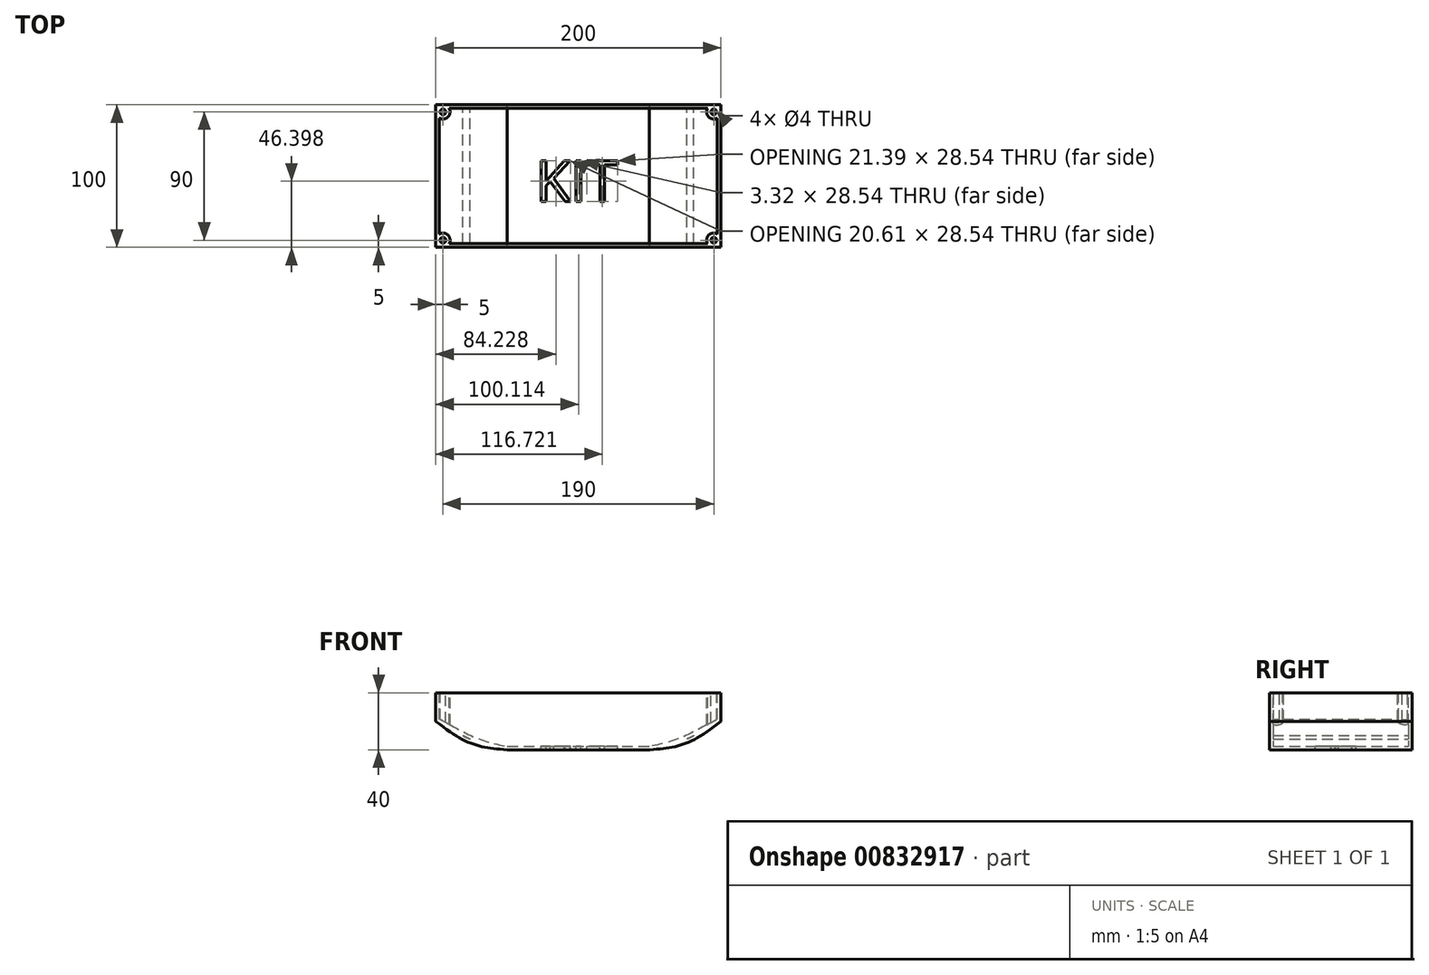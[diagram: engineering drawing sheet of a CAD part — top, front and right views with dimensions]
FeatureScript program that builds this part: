
annotation { "Feature Type Name" : "Feature", "Feature Type Description" : "" }
export const myFeature = defineFeature(function(context is Context, id is Id, definition is map)
    precondition{}
    {
        {
            var Q0;
            Q0=qCreatedBy(makeId("Front.planeOp"),FACE);
            var sketch = newSketch(context, id + "F0", { "sketchPlane" : qUnion([Q0])});
            skLineSegment(sketch, "E0.bottom", {"start": v(-100, 20) * mm, "end": v(100, 20) * mm});
            skLineSegment(sketch, "E0.top", {"start": v(-50, -20) * mm, "end": v(50, -20) * mm});
            skLineSegment(sketch, "E0.left", {"start": v(-100, 20) * mm, "end": v(-100, 0) * mm});
            skLineSegment(sketch, "E0.right", {"start": v(100, 20) * mm, "end": v(100, 0) * mm});
            skFitSpline(sketch, "E1", {"points": [v(-100, 0) * mm, v(-50, -20) * mm, v(50, -20) * mm, v(100, 0) * mm], "startDerivative": vector(217.09, -116.87) * mm, "endDerivative": vector(211.84, 170.9) * mm});
            skPoint(sketch, "E2.orphan", {"position": v(-100, -20) * mm});
            skPoint(sketch, "E3.orphan", {"position": v(100, -20) * mm});
            skSolve(sketch);
        }
        {
            var Q0;
            Q0=makeQuery(id+"F0.imprint","IMPRINT",FACE,{"disambiguationData":[TD([[makeQuery(id+"F0.imprint","IMPRINT",EDGE,{"derivedFrom":sQuery(id+"F0.wireOp",EDGE,"E0.bottom")}),-1.0]])]});
            extrude(context, id + "F1", {"entities" : qUnion([Q0]), "endBound" : BoundingType.SYMMETRIC, "depth" : 100 * mm, "offsetDistance" : 25 * mm});
        }
        {
            var Q0;
            Q0=makeQuery(id+"F1.opExtrude","SWEPT_FACE",FACE,{"disambiguationData":[OSD([sQuery(id+"F0.wireOp",EDGE,"E0.bottom")])]});
            shell(context, id + "F2", {"entities" : qUnion([Q0]), "thickness" : 2.5 * mm});
        }
        {
            var Q0;
            Q0=makeQuery(id+"F1.opExtrude","SWEPT_FACE",FACE,{"disambiguationData":[OSD([sQuery(id+"F0.wireOp",EDGE,"E0.bottom")])]});
            var sketch = newSketch(context, id + "F3", { "sketchPlane" : qUnion([Q0])});
            skCircle(sketch, "E4", {"center": v(-95, -45) * mm, "radius": 2 * mm});
            skCircle(sketch, "E5", {"center": v(-95, -45) * mm, "radius": 5 * mm});
            skSolve(sketch);
        }
        {
            var Q0;
            Q0 = qSketchRegion(id + "F3", true);
            extrude(context, id + "F4", {"entities" : qUnion([Q0]), "operationType" : NewBodyOperationType.ADD, "endBound" : BoundingType.UP_TO_NEXT, "oppositeDirection" : true, "depth" : 25 * mm, "offsetDistance" : 25 * mm});
        }
        {
            var Q0;
            Q0=makeQuery(id+"F1.opExtrude","SWEPT_BODY",BODY,{"disambiguationData":[OSD([sQuery(id+"F0.wireOp",EDGE,"E0.bottom"),sQuery(id+"F0.wireOp",EDGE,"E0.top"),sQuery(id+"F0.wireOp",EDGE,"E0.left"),sQuery(id+"F0.wireOp",EDGE,"E0.right"),sQuery(id+"F0.wireOp",EDGE,"E1"),sQuery(id+"F0.wireOp",EDGE,"E1")])]});
            var Q1;
            Q1=qCreatedBy(makeId("Right.planeOp"),FACE);
            mirror(context, id + "F5", {"operationType" : NewBodyOperationType.ADD, "entities" : qUnion([Q0]), "mirrorPlane" : qUnion([Q1])});
        }
        {
            var Q0;
            Q0=makeQuery(id+"F1.opExtrude","SWEPT_BODY",BODY,{"disambiguationData":[OSD([sQuery(id+"F0.wireOp",EDGE,"E0.bottom"),sQuery(id+"F0.wireOp",EDGE,"E0.top"),sQuery(id+"F0.wireOp",EDGE,"E0.left"),sQuery(id+"F0.wireOp",EDGE,"E0.right"),sQuery(id+"F0.wireOp",EDGE,"E1"),sQuery(id+"F0.wireOp",EDGE,"E1")])]});
            var Q1;
            Q1=qCreatedBy(makeId("Front.planeOp"),FACE);
            mirror(context, id + "F6", {"operationType" : NewBodyOperationType.ADD, "entities" : qUnion([Q0]), "mirrorPlane" : qUnion([Q1])});
        }
        {
            var Q0;
            Q0=makeQuery(id+"F2.opShell","OFFSET_FACE",FACE,{"disambiguationData":[OSD([sQuery(id+"F0.wireOp",EDGE,"E0.top")])]});
            var sketch = newSketch(context, id + "F7", { "sketchPlane" : qUnion([Q0])});
            skText(sketch, "E6", { "text": "KIT", "fontName": "OpenSans-Regular.ttf"});
            const initialGuessF7  = {"E6": [-0.03, -0.01787, 1, 0, 0.02878]};
            skSetInitialGuess(sketch, initialGuessF7);
            skSolve(sketch);
        }
        {
            var Q0;
            Q0 = qSketchRegion(id + "F7", true);
            extrude(context, id + "F8", {"entities" : qUnion([Q0]), "operationType" : NewBodyOperationType.REMOVE, "oppositeDirection" : true, "depth" : 25 * mm, "offsetDistance" : 25 * mm});
        }
    });
